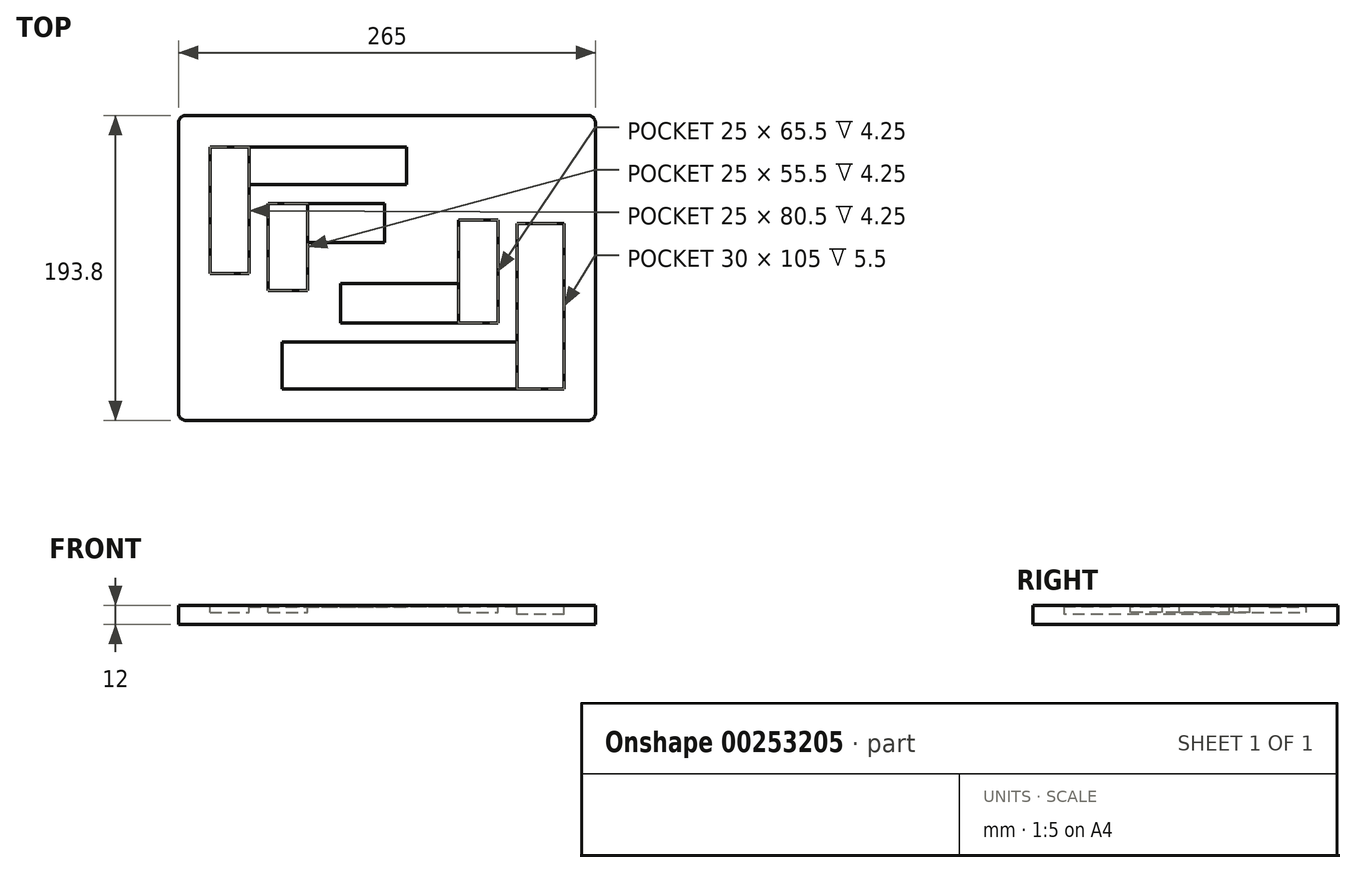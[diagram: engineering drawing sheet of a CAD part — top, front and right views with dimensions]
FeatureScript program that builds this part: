
annotation { "Feature Type Name" : "Feature", "Feature Type Description" : "" }
export const myFeature = defineFeature(function(context is Context, id is Id, definition is map)
    precondition{}
    {
        {
            var Q0;
            Q0=qCreatedBy(makeId("Top.planeOp"),FACE);
            var sketch = newSketch(context, id + "F0", { "sketchPlane" : qUnion([Q0])});
            skLineSegment(sketch, "E0", {"start": v(-125, 73.8) * mm, "end": v(-125, -6.7) * mm});
            skLineSegment(sketch, "E1", {"start": v(-125, -6.7) * mm, "end": v(-100, -6.7) * mm});
            skLineSegment(sketch, "E2", {"start": v(-100, -6.7) * mm, "end": v(-100, 50) * mm});
            skLineSegment(sketch, "E3", {"start": v(-100, 50) * mm, "end": v(0, 50) * mm});
            skLineSegment(sketch, "E4", {"start": v(0, 50) * mm, "end": v(0, 73.8) * mm});
            skLineSegment(sketch, "E5", {"start": v(-100, 50) * mm, "end": v(-100, 73.8) * mm});
            skLineSegment(sketch, "E6", {"start": v(-125, 73.8) * mm, "end": v(-100, 73.8) * mm});
            skLineSegment(sketch, "E7", {"start": v(-100, 73.8) * mm, "end": v(0, 73.8) * mm});
            skLineSegment(sketch, "E8.bottom", {"start": v(-88, 38) * mm, "end": v(-63, 38) * mm});
            skLineSegment(sketch, "E8.top", {"start": v(-88, -17.5) * mm, "end": v(-63, -17.5) * mm});
            skLineSegment(sketch, "E8.left", {"start": v(-88, 38) * mm, "end": v(-88, -17.5) * mm});
            skLineSegment(sketch, "E8.right", {"start": v(-63, 38) * mm, "end": v(-63, -17.5) * mm});
            skLineSegment(sketch, "E9.bottom", {"start": v(-63, 38) * mm, "end": v(-14, 38) * mm});
            skLineSegment(sketch, "E9.top", {"start": v(-63, 13) * mm, "end": v(-14, 13) * mm});
            skLineSegment(sketch, "E9.left", {"start": v(-63, 38) * mm, "end": v(-63, 13) * mm});
            skLineSegment(sketch, "E9.right", {"start": v(-14, 38) * mm, "end": v(-14, 13) * mm});
            skLineSegment(sketch, "E10.bottom", {"start": v(33, 27.5) * mm, "end": v(58, 27.5) * mm});
            skLineSegment(sketch, "E10.top", {"start": v(33, -38) * mm, "end": v(58, -38) * mm});
            skLineSegment(sketch, "E10.left", {"start": v(33, 27.5) * mm, "end": v(33, -38) * mm});
            skLineSegment(sketch, "E10.right", {"start": v(58, 27.5) * mm, "end": v(58, -38) * mm});
            skLineSegment(sketch, "E11.bottom", {"start": v(33, -38) * mm, "end": v(-42, -38) * mm});
            skLineSegment(sketch, "E11.top", {"start": v(33, -13) * mm, "end": v(-42, -13) * mm});
            skLineSegment(sketch, "E11.left", {"start": v(33, -38) * mm, "end": v(33, -13) * mm});
            skLineSegment(sketch, "E11.right", {"start": v(-42, -38) * mm, "end": v(-42, -13) * mm});
            skLineSegment(sketch, "E12.bottom", {"start": v(100, 25) * mm, "end": v(70, 25) * mm});
            skLineSegment(sketch, "E12.top", {"start": v(100, -80) * mm, "end": v(70, -80) * mm});
            skLineSegment(sketch, "E12.left", {"start": v(100, 25) * mm, "end": v(100, -80) * mm});
            skLineSegment(sketch, "E12.right", {"start": v(70, 25) * mm, "end": v(70, -80) * mm});
            skLineSegment(sketch, "E13.bottom", {"start": v(70, -80) * mm, "end": v(-79, -80) * mm});
            skLineSegment(sketch, "E13.top", {"start": v(70, -50) * mm, "end": v(-79, -50) * mm});
            skLineSegment(sketch, "E13.left", {"start": v(70, -80) * mm, "end": v(70, -50) * mm});
            skLineSegment(sketch, "E13.right", {"start": v(-79, -80) * mm, "end": v(-79, -50) * mm});
            skSolve(sketch);
        }
        {
            var Q0;
            Q0=qCreatedBy(makeId("Top.planeOp"),FACE);
            var sketch = newSketch(context, id + "F1", { "sketchPlane" : qUnion([Q0])});
            skLineSegment(sketch, "E14.bottom", {"start": v(-145, 93.8) * mm, "end": v(120, 93.8) * mm});
            skLineSegment(sketch, "E14.top", {"start": v(-145, -100) * mm, "end": v(120, -100) * mm});
            skLineSegment(sketch, "E14.left", {"start": v(-145, 93.8) * mm, "end": v(-145, -100) * mm});
            skLineSegment(sketch, "E14.right", {"start": v(120, 93.8) * mm, "end": v(120, -100) * mm});
            skSolve(sketch);
        }
        {
            var Q0;
            Q0=makeQuery(id+"F1.imprint","IMPRINT",FACE,{"disambiguationData":[TD([[makeQuery(id+"F1.imprint","IMPRINT",EDGE,{"derivedFrom":sQuery(id+"F1.wireOp",EDGE,"E14.bottom")}),-1.0]])]});
            extrude(context, id + "F2", {"entities" : qUnion([Q0]), "oppositeDirection" : true, "depth" : 12 * mm});
        }
        {
            var Q0;
            Q0 = qSketchRegion(id + "F0", true);
            extrude(context, id + "F3", {"entities" : qUnion([Q0]), "operationType" : NewBodyOperationType.REMOVE, "oppositeDirection" : true, "depth" : .8 * mm});
        }
        {
            var Q0;
            Q0=makeQuery(id+"F0.imprint","IMPRINT",FACE,{"disambiguationData":[TD([[makeQuery(id+"F0.imprint","IMPRINT",EDGE,{"derivedFrom":sQuery(id+"F0.wireOp",EDGE,"E10.bottom")}),-1.0]])]});
            var Q1;
            Q1=makeQuery(id+"F0.imprint","IMPRINT",FACE,{"disambiguationData":[TD([[makeQuery(id+"F0.imprint","IMPRINT",EDGE,{"derivedFrom":sQuery(id+"F0.wireOp",EDGE,"E8.bottom")}),-1.0]])]});
            var Q2;
            Q2=makeQuery(id+"F0.imprint","IMPRINT",FACE,{"disambiguationData":[TD([[makeQuery(id+"F0.imprint","IMPRINT",EDGE,{"derivedFrom":sQuery(id+"F0.wireOp",EDGE,"E0")}),1.0]])]});
            extrude(context, id + "F4", {"entities" : qUnion([Q0, Q1, Q2]), "operationType" : NewBodyOperationType.REMOVE, "oppositeDirection" : true, "depth" : 4.25 * mm});
        }
        {
            var Q0;
            Q0=makeQuery(id+"F0.imprint","IMPRINT",FACE,{"disambiguationData":[TD([[makeQuery(id+"F0.imprint","IMPRINT",EDGE,{"derivedFrom":sQuery(id+"F0.wireOp",EDGE,"E12.bottom")}),1.0]])]});
            extrude(context, id + "F5", {"entities" : qUnion([Q0]), "operationType" : NewBodyOperationType.REMOVE, "oppositeDirection" : true, "depth" : 5.5 * mm});
        }
        {
            var Q0;
            Q0=makeQuery(id+"F2.opExtrude","SWEPT_EDGE",EDGE,{"disambiguationData":[OSD([sQuery(id+"F1.wireOp",EDGE,"E14.top"),sQuery(id+"F1.wireOp",EDGE,"E14.left")])]});
            var Q1;
            Q1=makeQuery(id+"F2.opExtrude","SWEPT_EDGE",EDGE,{"disambiguationData":[OSD([sQuery(id+"F1.wireOp",EDGE,"E14.top"),sQuery(id+"F1.wireOp",EDGE,"E14.right")])]});
            var Q2;
            Q2=makeQuery(id+"F2.opExtrude","SWEPT_EDGE",EDGE,{"disambiguationData":[OSD([sQuery(id+"F1.wireOp",EDGE,"E14.bottom"),sQuery(id+"F1.wireOp",EDGE,"E14.right")])]});
            var Q3;
            Q3=makeQuery(id+"F2.opExtrude","SWEPT_EDGE",EDGE,{"disambiguationData":[OSD([sQuery(id+"F1.wireOp",EDGE,"E14.bottom"),sQuery(id+"F1.wireOp",EDGE,"E14.left")])]});
            fillet(context, id + "F6", {"entities" : qUnion([Q0, Q1, Q2, Q3]), "radius" : 5 * mm, "tangentPropagation" : true, "allowEdgeOverflow" : false});
        }
    });
